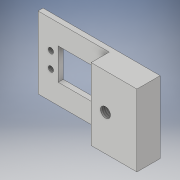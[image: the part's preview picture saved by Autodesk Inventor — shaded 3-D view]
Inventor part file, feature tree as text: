
AUTODESK INVENTOR PART (.ipt)
format: ipt  version: 2017 (Build 210142000, 142)  size: 191,488 bytes
history: native  units: in
note: dims shown in document units (in); Inventor stores cm internally (conversion verified against a paired STEP export)
features: sketch x11, extrude x8, thread x5, hole x1
ambient origin geometry x8: Origin, YZ Plane, XZ Plane, XY Plane, X Axis, Y Axis, Z Axis, Center Point
bodies: Solid1 (feature_tree)
feature tree (25):
  extrude  "Extrusion1"  Depth=0.78in
  extrude  "Extrusion2"  Depth=0.125in
  extrude  "Extrusion3"  Depth=0.125in
  extrude  "Extrusion4"  Depth=0.135in
  extrude  "Extrusion7"  Depth=0.125in TaperAngle=0.0deg
  sketch  "Sketch9"  dims[d21=0.125in d22=0.324in d23=0.0in d33=0.75in d34=0.324in d35=0.0in d36=1.78in d41=0.25in]
  extrude  "Extrusion9"  Depth=0.25in TaperAngle=0.0deg
  thread  "Thread1"  [1 undecoded]
  thread  "Thread2"  [1 undecoded]
  thread  "Thread3"  [1 undecoded]
  thread  "Thread4"  [1 undecoded]
  extrude  "Extrusion10"  Depth=0.2in
  sketch  "Sketch12"  dims[d50=1.0in d51=0.0in d52=1.0in d53=0.0in d54=1.0in d55=0.0in]
  hole  "Hole1"  [1 undecoded]
  extrude  "Extrusion11"  Depth=1.0in TaperAngle=0.0deg
  thread  "Thread5"  [1 undecoded]
  sketch  "Sketch1"  dims[d0=1.528in d1=0.78in]
  sketch  "Sketch2"  dims[d6=0.125in d7=0.0in d10=0.083in]
  sketch  "Sketch3"  dims[d11=0.125in d12=0.0in d15=0.135in]
  sketch  "Sketch4"  dims[d16=0.135in d17=0.135in]
  sketch  "Sketch8"  dims[d18=0.135in d19=0.125in d20=0.0in]
  sketch  "Sketch10"  dims[d44=0.2in d45=0.0in d46=1.949in]
  sketch  "Sketch11"  dims[d47=1.949in d48=1.0in d49=0.0in]
  sketch  "Sketch13"  dims[d56=0.5in]
  sketch  "Sketch14"  dims[d57=0.75in d58=0.126in d59=0.0in d60=0.356in d61=0.89in d62=0.25in d63=0.25in d64=0.75in d65=0.375in d66=0.25in d67=0.5635in d68=0.25in d69=0.0in d70=0.01in d71=0.0in d72=1.0in d73=0.0in]
note: 6 required parameter values undecoded (feature->parameter linkage not recoverable at this tier; creation-order binding heuristic only, values carry confidence <= 0.55)
